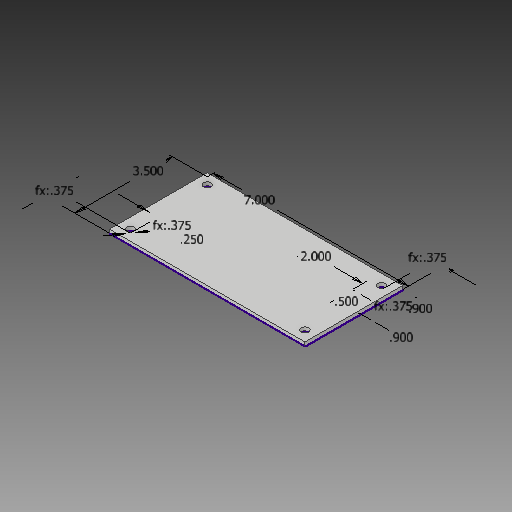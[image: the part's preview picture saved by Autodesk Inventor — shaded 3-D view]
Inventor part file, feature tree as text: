
AUTODESK INVENTOR PART (.ipt)
format: ipt  version: 2018 (Build 220112000, 112)  size: 117,248 bytes
history: native  units: in
note: dims shown in document units (in); Inventor stores cm internally (conversion verified against a paired STEP export)
features: sketch x3, extrude x2, hole x2
ambient origin geometry x8: Origin, YZ Plane, XZ Plane, XY Plane, X Axis, Y Axis, Z Axis, Center Point
bodies: Solid1 (feature_tree)
feature tree (7):
  sketch  "Sketch1"  dims[d0=7.0in d1=3.5in]
  extrude  "Extrusion1"  Depth=3.5in
  extrude  "Extrusion2"  Depth=0.9in
  sketch  "Sketch2"  dims[d2=0.9in d3=0.9in]
  hole  "Hole3"  [1 undecoded]
  sketch  "Sketch4"  dims[d4=0.5in d5=2.0in d6=0.125in d7=0.0in d8=0.6in d9=0.0in d10=0.375in d11=0.375in d12=0.375in d13=0.375in d14=0.25in d15=0.375in d16=0.375in d24=0.266in d25=0.75in d26=0.375in d27=0.25in d28=0.5635in d29=1.0in d30=0.0in]
  hole  "Hole2"  [1 undecoded]
note: 2 required parameter values undecoded (feature->parameter linkage not recoverable at this tier; creation-order binding heuristic only, values carry confidence <= 0.55)
